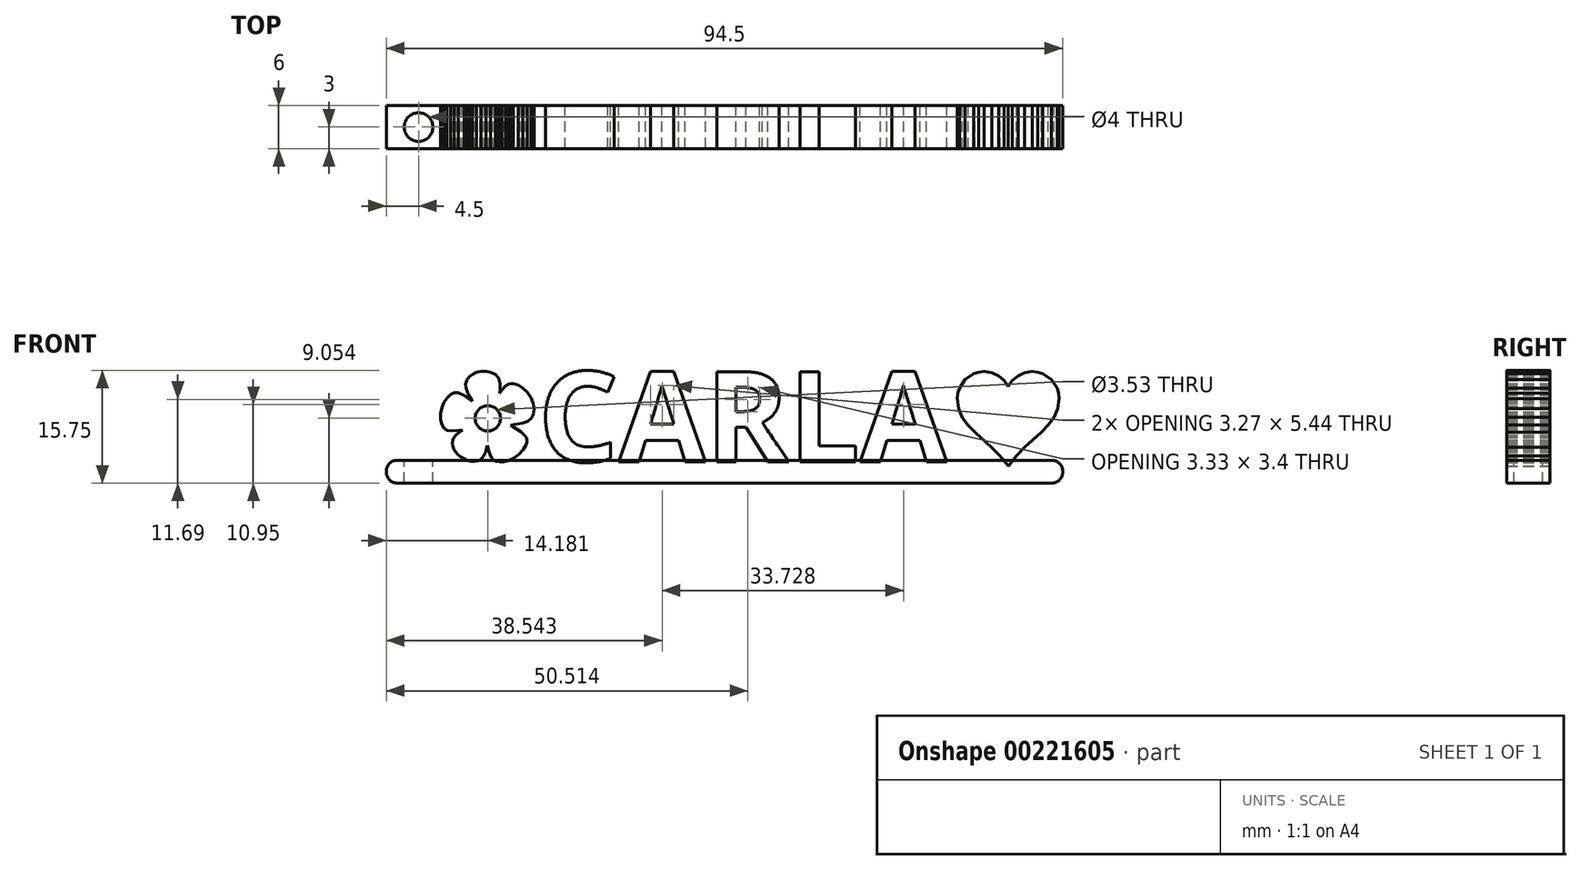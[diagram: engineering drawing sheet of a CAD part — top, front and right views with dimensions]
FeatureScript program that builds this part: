
annotation { "Feature Type Name" : "Feature", "Feature Type Description" : "" }
export const myFeature = defineFeature(function(context is Context, id is Id, definition is map)
    precondition{}
    {
        {
            var Q0;
            Q0=qCreatedBy(makeId("Front.planeOp"),FACE);
            var sketch = newSketch(context, id + "F0", { "sketchPlane" : qUnion([Q0])});
            skText(sketch, "E0", { "text": "   CARLA", "fontName": "OpenSans-Bold.ttf"});
            skLineSegment(sketch, "E1.0.0", {"start": v(-9.3, 0.1) * mm, "end": v(-8.53, 0.46) * mm});
            skLineSegment(sketch, "E1.0.1", {"start": v(-8.53, 0.46) * mm, "end": v(-7.79, 1.02) * mm});
            skLineSegment(sketch, "E1.0.2", {"start": v(-7.79, 1.02) * mm, "end": v(-7.18, 1.67) * mm});
            skLineSegment(sketch, "E1.0.3", {"start": v(-7.18, 1.67) * mm, "end": v(-6.78, 2.35) * mm});
            skLineSegment(sketch, "E1.0.4", {"start": v(-6.78, 2.35) * mm, "end": v(-6.68, 2.7) * mm});
            skLineSegment(sketch, "E1.0.5", {"start": v(-6.68, 2.7) * mm, "end": v(-6.67, 3.02) * mm});
            skLineSegment(sketch, "E1.0.6", {"start": v(-6.67, 3.02) * mm, "end": v(-6.73, 3.33) * mm});
            skLineSegment(sketch, "E1.0.7", {"start": v(-6.73, 3.33) * mm, "end": v(-6.89, 3.62) * mm});
            skLineSegment(sketch, "E1.0.8", {"start": v(-6.89, 3.62) * mm, "end": v(-7.48, 4.2) * mm});
            skLineSegment(sketch, "E1.0.9", {"start": v(-7.48, 4.2) * mm, "end": v(-8.5, 4.79) * mm});
            skLineSegment(sketch, "E1.0.10", {"start": v(-8.5, 4.79) * mm, "end": v(-8.93, 5.06) * mm});
            skLineSegment(sketch, "E1.0.11", {"start": v(-8.93, 5.06) * mm, "end": v(-8.42, 5.16) * mm});
            skLineSegment(sketch, "E1.0.12", {"start": v(-8.42, 5.16) * mm, "end": v(-7.31, 5.37) * mm});
            skLineSegment(sketch, "E1.0.13", {"start": v(-7.31, 5.37) * mm, "end": v(-6.55, 5.65) * mm});
            skLineSegment(sketch, "E1.0.14", {"start": v(-6.55, 5.65) * mm, "end": v(-6.05, 6.04) * mm});
            skLineSegment(sketch, "E1.0.15", {"start": v(-6.05, 6.04) * mm, "end": v(-5.76, 6.58) * mm});
            skLineSegment(sketch, "E1.0.16", {"start": v(-5.76, 6.58) * mm, "end": v(-5.64, 7.33) * mm});
            skLineSegment(sketch, "E1.0.17", {"start": v(-5.64, 7.33) * mm, "end": v(-5.78, 8.14) * mm});
            skLineSegment(sketch, "E1.0.18", {"start": v(-5.78, 8.14) * mm, "end": v(-6.1, 8.93) * mm});
            skLineSegment(sketch, "E1.0.19", {"start": v(-6.1, 8.93) * mm, "end": v(-6.6, 9.67) * mm});
            skLineSegment(sketch, "E1.0.20", {"start": v(-6.6, 9.67) * mm, "end": v(-7.2, 10.28) * mm});
            skLineSegment(sketch, "E1.0.21", {"start": v(-7.2, 10.28) * mm, "end": v(-7.86, 10.72) * mm});
            skLineSegment(sketch, "E1.0.22", {"start": v(-7.86, 10.72) * mm, "end": v(-8.55, 10.93) * mm});
            skLineSegment(sketch, "E1.0.23", {"start": v(-8.55, 10.93) * mm, "end": v(-8.88, 10.93) * mm});
            skLineSegment(sketch, "E1.0.24", {"start": v(-8.88, 10.93) * mm, "end": v(-9.2, 10.85) * mm});
            skLineSegment(sketch, "E1.0.25", {"start": v(-9.2, 10.85) * mm, "end": v(-9.65, 10.56) * mm});
            skLineSegment(sketch, "E1.0.26", {"start": v(-9.65, 10.56) * mm, "end": v(-10.14, 9.98) * mm});
            skLineSegment(sketch, "E1.0.27", {"start": v(-10.14, 9.98) * mm, "end": v(-10.45, 9.58) * mm});
            skLineSegment(sketch, "E1.0.28", {"start": v(-10.45, 9.58) * mm, "end": v(-10.4, 10.03) * mm});
            skLineSegment(sketch, "E1.0.29", {"start": v(-10.4, 10.03) * mm, "end": v(-10.4, 10.93) * mm});
            skLineSegment(sketch, "E1.0.30", {"start": v(-10.4, 10.93) * mm, "end": v(-10.6, 11.63) * mm});
            skLineSegment(sketch, "E1.0.31", {"start": v(-10.6, 11.63) * mm, "end": v(-11.04, 12.15) * mm});
            skLineSegment(sketch, "E1.0.32", {"start": v(-11.04, 12.15) * mm, "end": v(-11.71, 12.5) * mm});
            skLineSegment(sketch, "E1.0.33", {"start": v(-11.71, 12.5) * mm, "end": v(-12.4, 12.64) * mm});
            skLineSegment(sketch, "E1.0.34", {"start": v(-12.4, 12.64) * mm, "end": v(-13.07, 12.62) * mm});
            skLineSegment(sketch, "E1.0.35", {"start": v(-13.07, 12.62) * mm, "end": v(-13.7, 12.47) * mm});
            skLineSegment(sketch, "E1.0.36", {"start": v(-13.7, 12.47) * mm, "end": v(-14.26, 12.2) * mm});
            skLineSegment(sketch, "E1.0.37", {"start": v(-14.26, 12.2) * mm, "end": v(-14.72, 11.83) * mm});
            skLineSegment(sketch, "E1.0.38", {"start": v(-14.72, 11.83) * mm, "end": v(-15.05, 11.38) * mm});
            skLineSegment(sketch, "E1.0.39", {"start": v(-15.05, 11.38) * mm, "end": v(-15.22, 10.87) * mm});
            skLineSegment(sketch, "E1.0.40", {"start": v(-15.22, 10.87) * mm, "end": v(-15.2, 10.3) * mm});
            skLineSegment(sketch, "E1.0.41", {"start": v(-15.2, 10.3) * mm, "end": v(-14.83, 9.4) * mm});
            skLineSegment(sketch, "E1.0.42", {"start": v(-14.83, 9.4) * mm, "end": v(-14.35, 8.55) * mm});
            skLineSegment(sketch, "E1.0.43", {"start": v(-14.35, 8.55) * mm, "end": v(-14.3, 8.4) * mm});
            skLineSegment(sketch, "E1.0.44", {"start": v(-14.3, 8.4) * mm, "end": v(-14.48, 8.53) * mm});
            skLineSegment(sketch, "E1.0.45", {"start": v(-14.48, 8.53) * mm, "end": v(-15.4, 9.23) * mm});
            skLineSegment(sketch, "E1.0.46", {"start": v(-15.4, 9.23) * mm, "end": v(-16.22, 9.63) * mm});
            skLineSegment(sketch, "E1.0.47", {"start": v(-16.22, 9.63) * mm, "end": v(-16.8, 9.63) * mm});
            skLineSegment(sketch, "E1.0.48", {"start": v(-16.8, 9.63) * mm, "end": v(-17.36, 9.37) * mm});
            skLineSegment(sketch, "E1.0.49", {"start": v(-17.36, 9.37) * mm, "end": v(-17.85, 8.9) * mm});
            skLineSegment(sketch, "E1.0.50", {"start": v(-17.85, 8.9) * mm, "end": v(-18.26, 8.26) * mm});
            skLineSegment(sketch, "E1.0.51", {"start": v(-18.26, 8.26) * mm, "end": v(-18.56, 7.51) * mm});
            skLineSegment(sketch, "E1.0.52", {"start": v(-18.56, 7.51) * mm, "end": v(-18.72, 6.71) * mm});
            skLineSegment(sketch, "E1.0.53", {"start": v(-18.72, 6.71) * mm, "end": v(-18.72, 5.9) * mm});
            skLineSegment(sketch, "E1.0.54", {"start": v(-18.72, 5.9) * mm, "end": v(-18.52, 5.16) * mm});
            skLineSegment(sketch, "E1.0.55", {"start": v(-18.52, 5.16) * mm, "end": v(-18.2, 4.64) * mm});
            skLineSegment(sketch, "E1.0.56", {"start": v(-18.2, 4.64) * mm, "end": v(-17.75, 4.36) * mm});
            skLineSegment(sketch, "E1.0.57", {"start": v(-17.75, 4.36) * mm, "end": v(-17.1, 4.27) * mm});
            skLineSegment(sketch, "E1.0.58", {"start": v(-17.1, 4.27) * mm, "end": v(-16.21, 4.37) * mm});
            skLineSegment(sketch, "E1.0.59", {"start": v(-16.21, 4.37) * mm, "end": v(-15.7, 4.43) * mm});
            skLineSegment(sketch, "E1.0.60", {"start": v(-15.7, 4.43) * mm, "end": v(-15.67, 4.4) * mm});
            skLineSegment(sketch, "E1.0.61", {"start": v(-15.67, 4.4) * mm, "end": v(-15.78, 4.33) * mm});
            skLineSegment(sketch, "E1.0.62", {"start": v(-15.78, 4.33) * mm, "end": v(-16.17, 4.07) * mm});
            skLineSegment(sketch, "E1.0.63", {"start": v(-16.17, 4.07) * mm, "end": v(-16.55, 3.71) * mm});
            skLineSegment(sketch, "E1.0.64", {"start": v(-16.55, 3.71) * mm, "end": v(-16.87, 3.33) * mm});
            skLineSegment(sketch, "E1.0.65", {"start": v(-16.87, 3.33) * mm, "end": v(-17.04, 3) * mm});
            skLineSegment(sketch, "E1.0.66", {"start": v(-17.04, 3) * mm, "end": v(-17.08, 2.6) * mm});
            skLineSegment(sketch, "E1.0.67", {"start": v(-17.08, 2.6) * mm, "end": v(-17.02, 2.2) * mm});
            skLineSegment(sketch, "E1.0.68", {"start": v(-17.02, 2.2) * mm, "end": v(-16.87, 1.78) * mm});
            skLineSegment(sketch, "E1.0.69", {"start": v(-16.87, 1.78) * mm, "end": v(-16.62, 1.39) * mm});
            skLineSegment(sketch, "E1.0.70", {"start": v(-16.62, 1.39) * mm, "end": v(-16.3, 1.02) * mm});
            skLineSegment(sketch, "E1.0.71", {"start": v(-16.3, 1.02) * mm, "end": v(-15.9, 0.69) * mm});
            skLineSegment(sketch, "E1.0.72", {"start": v(-15.9, 0.69) * mm, "end": v(-15.45, 0.4) * mm});
            skLineSegment(sketch, "E1.0.73", {"start": v(-15.45, 0.4) * mm, "end": v(-14.95, 0.2) * mm});
            skLineSegment(sketch, "E1.0.74", {"start": v(-14.95, 0.2) * mm, "end": v(-14.44, 0.06) * mm});
            skLineSegment(sketch, "E1.0.75", {"start": v(-14.44, 0.06) * mm, "end": v(-13.98, 0.02) * mm});
            skLineSegment(sketch, "E1.0.76", {"start": v(-13.98, 0.02) * mm, "end": v(-13.58, 0.08) * mm});
            skLineSegment(sketch, "E1.0.77", {"start": v(-13.58, 0.08) * mm, "end": v(-13.23, 0.23) * mm});
            skLineSegment(sketch, "E1.0.78", {"start": v(-13.23, 0.23) * mm, "end": v(-12.92, 0.49) * mm});
            skLineSegment(sketch, "E1.0.79", {"start": v(-12.92, 0.49) * mm, "end": v(-12.67, 0.84) * mm});
            skLineSegment(sketch, "E1.0.80", {"start": v(-12.67, 0.84) * mm, "end": v(-12.46, 1.28) * mm});
            skLineSegment(sketch, "E1.0.81", {"start": v(-12.46, 1.28) * mm, "end": v(-12.3, 1.83) * mm});
            skLineSegment(sketch, "E1.0.82", {"start": v(-12.3, 1.83) * mm, "end": v(-12.19, 2.26) * mm});
            skLineSegment(sketch, "E1.0.83", {"start": v(-12.19, 2.26) * mm, "end": v(-12.13, 2.1) * mm});
            skLineSegment(sketch, "E1.0.84", {"start": v(-12.13, 2.1) * mm, "end": v(-12.01, 1.53) * mm});
            skLineSegment(sketch, "E1.0.85", {"start": v(-12.01, 1.53) * mm, "end": v(-11.82, 1) * mm});
            skLineSegment(sketch, "E1.0.86", {"start": v(-11.82, 1) * mm, "end": v(-11.6, 0.55) * mm});
            skLineSegment(sketch, "E1.0.87", {"start": v(-11.6, 0.55) * mm, "end": v(-11.35, 0.26) * mm});
            skLineSegment(sketch, "E1.0.88", {"start": v(-11.35, 0.26) * mm, "end": v(-10.95, 0.05) * mm});
            skLineSegment(sketch, "E1.0.89", {"start": v(-10.95, 0.05) * mm, "end": v(-10.46, -0.04) * mm});
            skLineSegment(sketch, "E1.0.90", {"start": v(-10.46, -0.04) * mm, "end": v(-9.9, -0.03) * mm});
            skLineSegment(sketch, "E1.0.91", {"start": v(-9.9, -0.03) * mm, "end": v(-9.3, 0.1) * mm});
            skCircle(sketch, "E2", {"center": v(-12.12, 6.05) * mm, "radius": 1.77 * mm});
            skLineSegment(sketch, "E3", {"start": v(57.24, 12.6) * mm, "end": v(56.48, 12.52) * mm});
            skLineSegment(sketch, "E4", {"start": v(56.48, 12.52) * mm, "end": v(55.78, 12.3) * mm});
            skLineSegment(sketch, "E5", {"start": v(55.78, 12.3) * mm, "end": v(54.58, 11.5) * mm});
            skLineSegment(sketch, "E6", {"start": v(54.58, 11.5) * mm, "end": v(53.77, 10.3) * mm});
            skLineSegment(sketch, "E7", {"start": v(53.77, 10.3) * mm, "end": v(53.55, 9.59) * mm});
            skLineSegment(sketch, "E8", {"start": v(53.55, 9.59) * mm, "end": v(53.48, 8.83) * mm});
            skLineSegment(sketch, "E9", {"start": v(53.48, 8.83) * mm, "end": v(53.66, 7.39) * mm});
            skLineSegment(sketch, "E10", {"start": v(53.66, 7.39) * mm, "end": v(54.19, 6.16) * mm});
            skLineSegment(sketch, "E11", {"start": v(54.19, 6.16) * mm, "end": v(54.97, 5.08) * mm});
            skLineSegment(sketch, "E12", {"start": v(54.97, 5.08) * mm, "end": v(55.95, 4.08) * mm});
            skLineSegment(sketch, "E13", {"start": v(55.95, 4.08) * mm, "end": v(58.25, 2.03) * mm});
            skLineSegment(sketch, "E14", {"start": v(58.25, 2.03) * mm, "end": v(59.44, 0.82) * mm});
            skLineSegment(sketch, "E15", {"start": v(59.44, 0.82) * mm, "end": v(60.56, -0.59) * mm});
            skLineSegment(sketch, "E16", {"start": v(60.56, -0.59) * mm, "end": v(60.6, -0.65) * mm});
            skLineSegment(sketch, "E17", {"start": v(60.6, -0.65) * mm, "end": v(60.65, -0.59) * mm});
            skLineSegment(sketch, "E18", {"start": v(60.65, -0.59) * mm, "end": v(61.72, 0.82) * mm});
            skLineSegment(sketch, "E19", {"start": v(61.72, 0.82) * mm, "end": v(62.89, 2.03) * mm});
            skLineSegment(sketch, "E20", {"start": v(62.89, 2.03) * mm, "end": v(65.2, 4.12) * mm});
            skLineSegment(sketch, "E21", {"start": v(65.2, 4.12) * mm, "end": v(66.2, 5.13) * mm});
            skLineSegment(sketch, "E22", {"start": v(66.2, 5.13) * mm, "end": v(67, 6.21) * mm});
            skLineSegment(sketch, "E23", {"start": v(67, 6.21) * mm, "end": v(67.53, 7.42) * mm});
            skLineSegment(sketch, "E24", {"start": v(67.53, 7.42) * mm, "end": v(67.73, 8.83) * mm});
            skLineSegment(sketch, "E25", {"start": v(67.73, 8.83) * mm, "end": v(67.65, 9.59) * mm});
            skLineSegment(sketch, "E26", {"start": v(67.65, 9.59) * mm, "end": v(67.43, 10.3) * mm});
            skLineSegment(sketch, "E27", {"start": v(67.43, 10.3) * mm, "end": v(66.62, 11.5) * mm});
            skLineSegment(sketch, "E28", {"start": v(66.62, 11.5) * mm, "end": v(65.43, 12.3) * mm});
            skLineSegment(sketch, "E29", {"start": v(65.43, 12.3) * mm, "end": v(64.72, 12.52) * mm});
            skLineSegment(sketch, "E30", {"start": v(64.72, 12.52) * mm, "end": v(63.96, 12.6) * mm});
            skLineSegment(sketch, "E31", {"start": v(63.96, 12.6) * mm, "end": v(62.9, 12.44) * mm});
            skLineSegment(sketch, "E32", {"start": v(62.9, 12.44) * mm, "end": v(61.96, 12.01) * mm});
            skLineSegment(sketch, "E33", {"start": v(61.96, 12.01) * mm, "end": v(61.18, 11.35) * mm});
            skLineSegment(sketch, "E34", {"start": v(61.18, 11.35) * mm, "end": v(60.6, 10.5) * mm});
            skLineSegment(sketch, "E35", {"start": v(60.6, 10.5) * mm, "end": v(60.02, 11.35) * mm});
            skLineSegment(sketch, "E36", {"start": v(60.02, 11.35) * mm, "end": v(59.24, 12.01) * mm});
            skLineSegment(sketch, "E37", {"start": v(59.24, 12.01) * mm, "end": v(58.3, 12.44) * mm});
            skLineSegment(sketch, "E38", {"start": v(58.3, 12.44) * mm, "end": v(57.24, 12.6) * mm});
            skLineSegment(sketch, "E39", {"start": v(53.2, 12.68) * mm, "end": v(73.63, 12.68) * mm, "construction": true});
            const initialGuessF0  = {"E0": [-0.0188, 0, 1, 0, 0.01268]};
            skSetInitialGuess(sketch, initialGuessF0);
            skSolve(sketch);
        }
        {
            var Q0;
            Q0=qSketchRegion(id+"F0",true);
            extrude(context, id + "F1", {"entities" : qUnion([Q0]), "endBound" : BoundingType.SYMMETRIC, "depth" : 6 * mm});
        }
        {
            var Q0;
            Q0=qCreatedBy(makeId("Top.planeOp"),FACE);
            var sketch = newSketch(context, id + "F2", { "sketchPlane" : qUnion([Q0])});
            skLineSegment(sketch, "E40.bottom", {"start": v(-18.8, 3) * mm, "end": v(68.2, 3) * mm});
            skLineSegment(sketch, "E40.top", {"start": v(-18.8, -3) * mm, "end": v(68.2, -3) * mm});
            skLineSegment(sketch, "E40.left", {"start": v(-18.8, 3) * mm, "end": v(-18.8, -3) * mm});
            skLineSegment(sketch, "E40.right", {"start": v(68.2, 3) * mm, "end": v(68.2, -3) * mm});
            skSolve(sketch);
        }
        {
            var Q0;
            Q0=makeQuery(id+"F2.imprint","IMPRINT",FACE,{"disambiguationData":[TD([[makeQuery(id+"F2.imprint","IMPRINT",EDGE,{"derivedFrom":sQuery(id+"F2.wireOp",EDGE,"E40.bottom")}),-1.0]])]});
            extrude(context, id + "F3", {"entities" : qUnion([Q0]), "depth" : 0.2 * mm});
        }
        {
            var Q0;
            Q0=makeQuery(id+"F3.opExtrude","CAP_FACE",FACE,{"disambiguationData":[OSD([sQuery(id+"F2.wireOp",EDGE,"E40.bottom"),sQuery(id+"F2.wireOp",EDGE,"E40.top"),sQuery(id+"F2.wireOp",EDGE,"E40.left"),sQuery(id+"F2.wireOp",EDGE,"E40.right")])],"isStart":true});
            extrude(context, id + "F4", {"entities" : qUnion([Q0]), "depth" : 3 * mm});
        }
        {
            var Q0;
            {var subQ0=sQuery(id+"F2.wireOp",EDGE,"E40.left");Q0=makeQuery(id+"FaVoHrOpcFZXiYX_6.opBoolean","MERGE",FACE,{"derivedFrom":[makeQuery(id+"F3.opExtrude","SWEPT_FACE",FACE,{"disambiguationData":[OSD([subQ0])]}),makeQuery(id+"F4.opExtrude","SWEPT_FACE",FACE,{"disambiguationData":[OSD([subQ0])]})]});}
            var sketch = newSketch(context, id + "F5", { "sketchPlane" : qUnion([Q0])});
            skLineSegment(sketch, "E41.bottom", {"start": v(-3, -3) * mm, "end": v(3, -3) * mm});
            skLineSegment(sketch, "E41.top", {"start": v(-3, 0.2) * mm, "end": v(3, 0.2) * mm});
            skLineSegment(sketch, "E41.left", {"start": v(-3, -3) * mm, "end": v(-3, 0.2) * mm});
            skLineSegment(sketch, "E41.right", {"start": v(3, -3) * mm, "end": v(3, 0.2) * mm});
            skSolve(sketch);
        }
        {
            var Q0;
            Q0=qSketchRegion(id+"F5",true);
            extrude(context, id + "F6", {"entities" : qUnion([Q0]), "operationType" : NewBodyOperationType.ADD, "depth" : 7.5 * mm});
        }
        {
            var Q0;
            Q0=makeQuery(id+"F6.opExtrude","CAP_EDGE",EDGE,{"disambiguationData":[OSD([sQuery(id+"F5.wireOp",EDGE,"E41.bottom")])],"isStart":false});
            var Q1;
            Q1=makeQuery(id+"F6.opExtrude","CAP_EDGE",EDGE,{"disambiguationData":[OSD([sQuery(id+"F5.wireOp",EDGE,"E41.top")])],"isStart":false});
            var Q2;
            Q2=makeQuery(id+"F4.opExtrude","CAP_EDGE",EDGE,{"disambiguationData":[OSD([sQuery(id+"F2.wireOp",EDGE,"E40.right")])],"isStart":false});
            fillet(context, id + "F7", {"entities" : qUnion([Q0, Q1, Q2]), "radius" : 1.5 * mm, "tangentPropagation" : true, "allowEdgeOverflow" : false});
        }
        {
            var Q0;
            {var subQ19=sQuery(id+"F2.wireOp",EDGE,"E40.top");var subQ20=sQuery(id+"F2.wireOp",EDGE,"E40.bottom");var subQ63=sQuery(id+"F0.wireOp",EDGE,"E0.sketch_text.stroke-2");var subQ66=sQuery(id+"F2.wireOp",EDGE,"E40.left");Q0=makeQuery(id+"F6.boolean.opBoolean","MERGE",FACE,{"derivedFrom":[makeQuery(id+"FaVoHrOpcFZXiYX_6.opBoolean","SPLIT",FACE,{"disambiguationData":[TD([makeQuery(id+"F1.opExtrude","SWEPT_FACE",FACE,{"disambiguationData":[OSD([subQ63])]})])],"derivedFrom":makeQuery(id+"F3.opExtrude","CAP_FACE",FACE,{"disambiguationData":[OSD([subQ20,subQ19,subQ66,sQuery(id+"F2.wireOp",EDGE,"E40.right")])],"isStart":false})}),makeQuery(id+"F6.opExtrude","SWEPT_FACE",FACE,{"disambiguationData":[OSD([sQuery(id+"F5.wireOp",EDGE,"E41.top")])]})]});}
            var sketch = newSketch(context, id + "F8", { "sketchPlane" : qUnion([Q0])});
            skCircle(sketch, "E42", {"center": v(-21.8, 0) * mm, "radius": 2 * mm});
            skSolve(sketch);
        }
        {
            var Q0;
            Q0=makeQuery(id+"F8.imprint","IMPRINT",FACE,{"disambiguationData":[TD([[makeQuery(id+"F8.imprint","IMPRINT",EDGE,{"derivedFrom":sQuery(id+"F8.wireOp",EDGE,"E42")}),1.0]])]});
            extrude(context, id + "F9", {"entities" : qUnion([Q0]), "operationType" : NewBodyOperationType.REMOVE, "oppositeDirection" : true, "depth" : 4 * mm});
        }
        {
            var Q0;
            Q0=makeQuery(id+"F3.opExtrude","CAP_EDGE",EDGE,{"disambiguationData":[OSD([sQuery(id+"F2.wireOp",EDGE,"E40.right")])],"isStart":false});
            fillet(context, id + "F10", {"entities" : qUnion([Q0]), "radius" : 1.5 * mm, "tangentPropagation" : true, "allowEdgeOverflow" : false});
        }
    });
